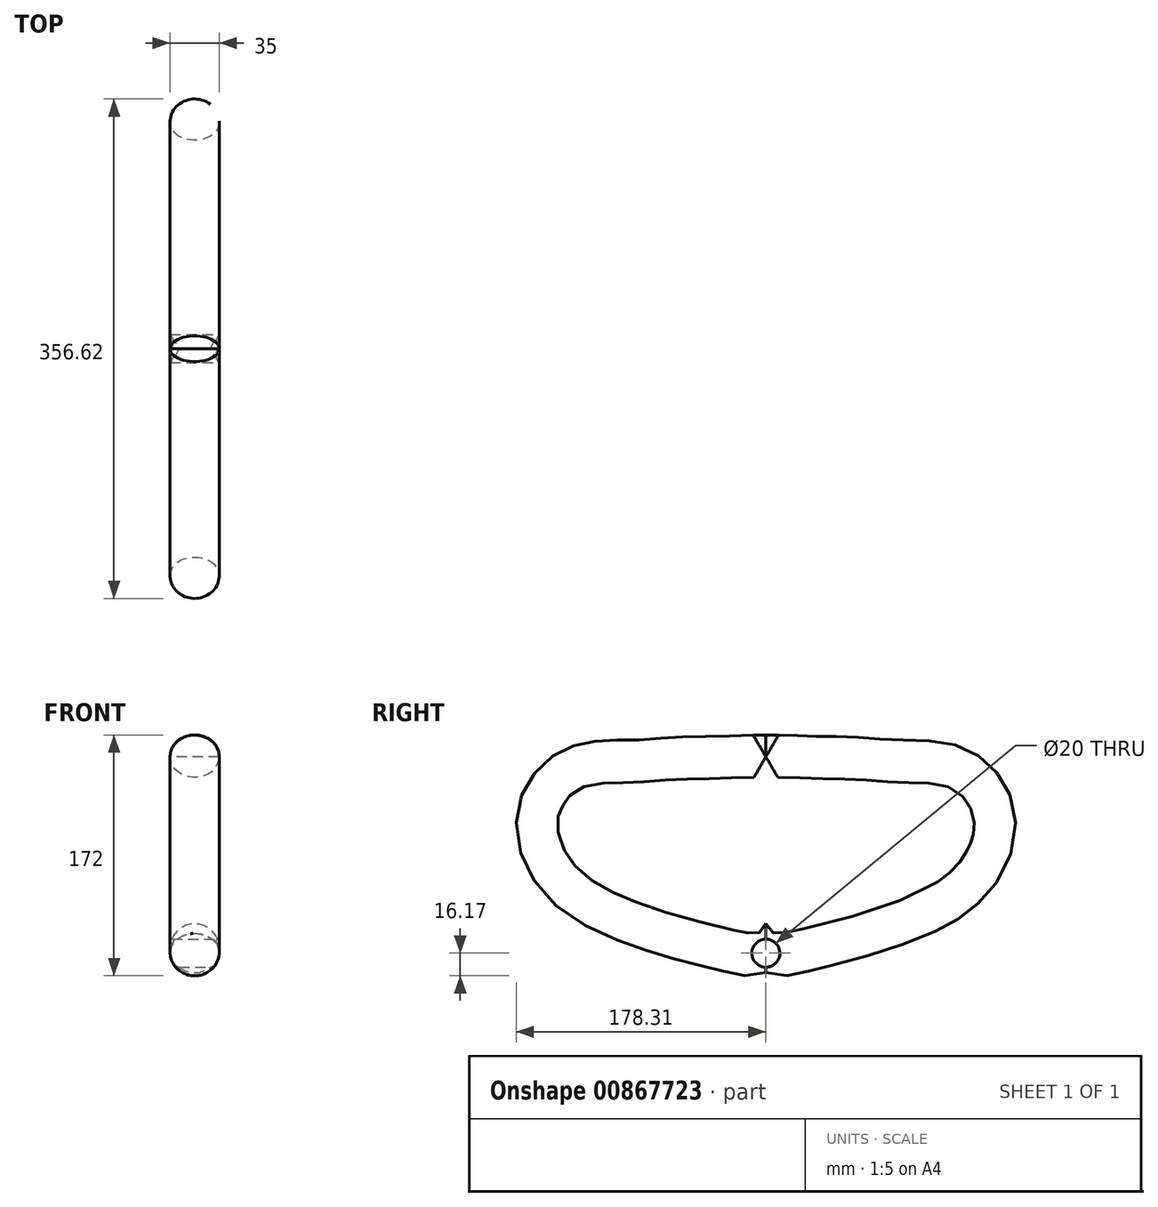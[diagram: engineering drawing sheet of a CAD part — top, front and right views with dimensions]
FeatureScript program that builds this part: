
annotation { "Feature Type Name" : "Feature", "Feature Type Description" : "" }
export const myFeature = defineFeature(function(context is Context, id is Id, definition is map)
    precondition{}
    {
        {
            var Q0;
            Q0=qCreatedBy(makeId("Front.planeOp"),FACE);
            var sketch = newSketch(context, id + "F0", { "sketchPlane" : qUnion([Q0])});
            skCircle(sketch, "E0", {"center": v(0, -73.58) * mm, "radius": 17.5 * mm});
            skSolve(sketch);
        }
        {
            var Q0;
            Q0=qCreatedBy(makeId("Right.planeOp"),FACE);
            var sketch = newSketch(context, id + "F1", { "sketchPlane" : qUnion([Q0])});
            skFitSpline(sketch, "E1", {"points": [v(0, -72.99) * mm, v(-28.36, -74.18) * mm, v(-126.59, -40.45) * mm, v(-159.9, 0) * mm, v(-159.46, 29.16) * mm, v(-143.11, 50.1) * mm, v(-121.46, 58.01) * mm, v(-92.73, 59.68) * mm, v(-65.67, 61.34) * mm, v(-39.44, 62.18) * mm, v(0, 63.08) * mm], "startDerivative": vector(-298.25, -176.99) * mm, "endDerivative": vector(385.58, 3.38) * mm});
            skLineSegment(sketch, "E2", {"start": v(0, 63.08) * mm, "end": v(8.41, 63.08) * mm});
            skSolve(sketch);
        }
        {
            var Q0;
            Q0=makeQuery(id+"F0.imprint","IMPRINT",FACE,{"disambiguationData":[TD([[makeQuery(id+"F0.imprint","IMPRINT",EDGE,{"derivedFrom":sQuery(id+"F0.wireOp",EDGE,"E0")}),1.0]])]});
            var Q1;
            Q1=sQuery(id+"F1.wireOp",EDGE,"E1");
            sweep(context, id + "F2", {"profiles" : qUnion([Q0]), "path" : qUnion([Q1])});
        }
        {
            var Q0;
            Q0=makeQuery(id+"F2.opSweep","SWEPT_BODY",BODY,{"disambiguationData":[OSD([sQuery(id+"F0.wireOp",EDGE,"E0"),sQuery(id+"F1.wireOp",EDGE,"E1")])]});
            var Q1;
            Q1=qCreatedBy(makeId("Front.planeOp"),FACE);
            mirror(context, id + "F3", {"operationType" : NewBodyOperationType.ADD, "entities" : qUnion([Q0]), "mirrorPlane" : qUnion([Q1])});
        }
        {
            var Q0;
            Q0=qCreatedBy(makeId("Right.planeOp"),FACE);
            var sketch = newSketch(context, id + "F4", { "sketchPlane" : qUnion([Q0])});
            skCircle(sketch, "E3", {"center": v(0, -77.1) * mm, "radius": 10 * mm});
            skSolve(sketch);
        }
        {
            var Q0;
            Q0 = qSketchRegion(id + "F4", true);
            extrude(context, id + "F5", {"entities" : qUnion([Q0]), "operationType" : NewBodyOperationType.REMOVE, "oppositeDirection" : true, "depth" : 25 * mm, "offsetDistance" : 25 * mm, "hasSecondDirection" : true, "secondDirectionOppositeDirection" : false, "secondDirectionDepth" : 25 * mm});
        }
    });
